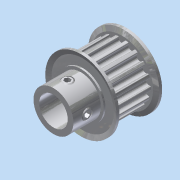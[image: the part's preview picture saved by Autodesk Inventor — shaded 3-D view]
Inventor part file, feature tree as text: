
AUTODESK INVENTOR PART (.ipt)
format: ipt  version: 2015 (Build 190159000, 159)  size: 324,608 bytes
history: native  units: in
note: dims shown in document units (in); Inventor stores cm internally (conversion verified against a paired STEP export)
features: other x1, extrude x1, imported_body x1, sketch x1
ambient origin geometry x8: Origin, YZ Plane, XZ Plane, XY Plane, X Axis, Y Axis, Z Axis, Center Point
bodies: Solid1 (feature_tree)
feature tree (4):
  other  "a_6a23m018df09061"
  extrude  "Extrusion1"  Depth=0.3937in TaperAngle=0.0deg
  imported_body  "Base1"
  sketch  "Sketch1"  dims[d0=0.315in d1=0.3937in d2=0.0in]
